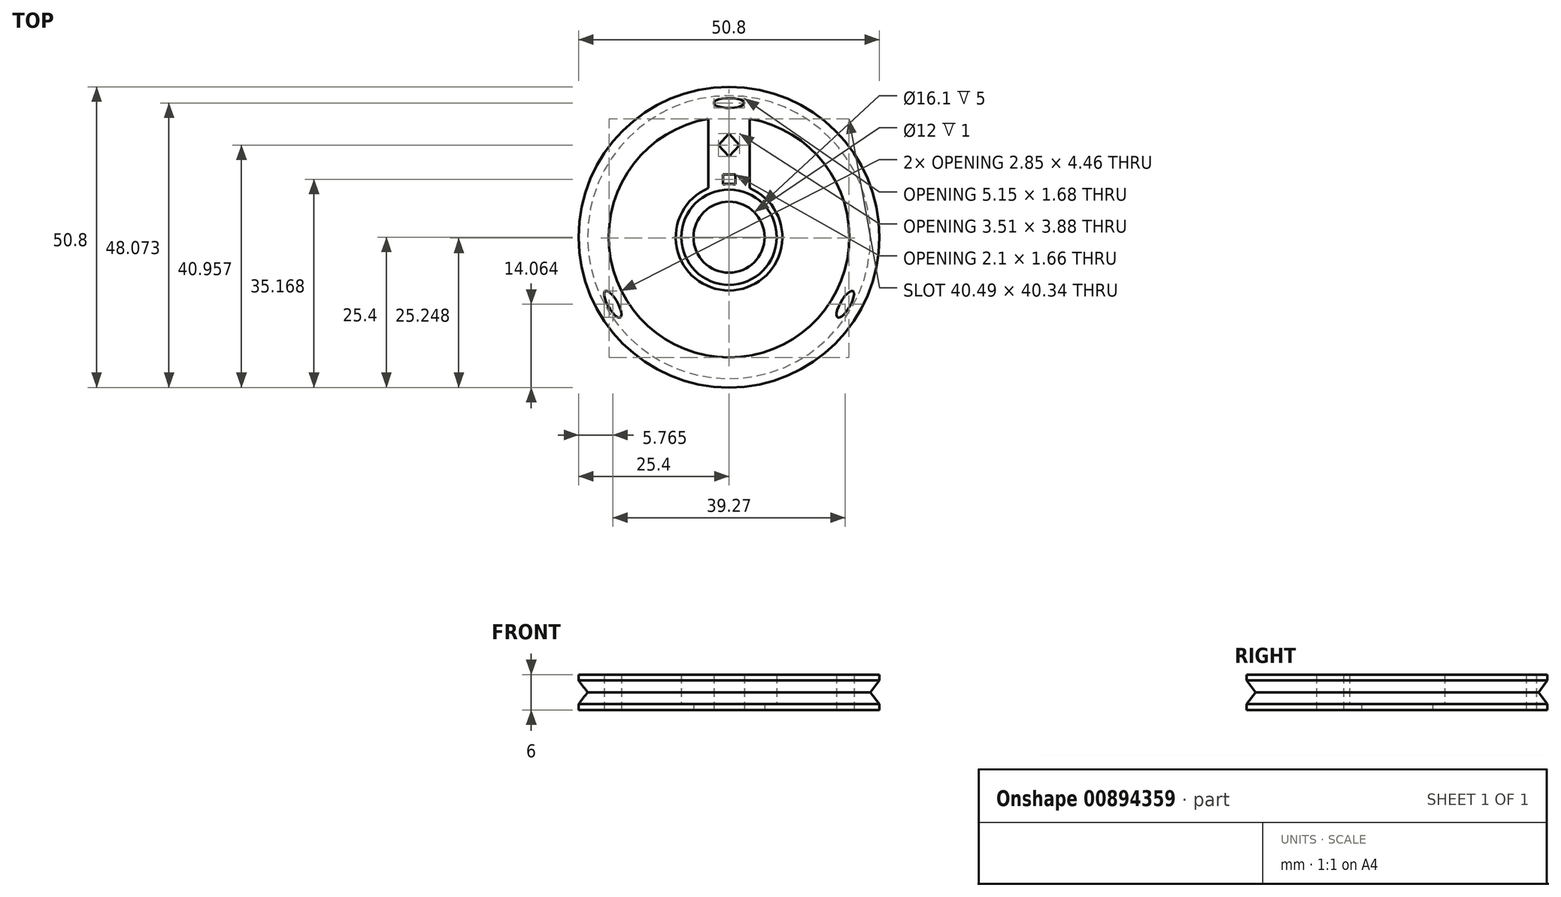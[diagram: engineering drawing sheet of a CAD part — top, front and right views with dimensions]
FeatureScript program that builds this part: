
annotation { "Feature Type Name" : "Feature", "Feature Type Description" : "" }
export const myFeature = defineFeature(function(context is Context, id is Id, definition is map)
    precondition{}
    {
        {
            var Q0;
            Q0=qCreatedBy(makeId("Top.planeOp"),FACE);
            var sketch = newSketch(context, id + "F0", { "sketchPlane" : qUnion([Q0])});
            skCircle(sketch, "E0", {"center": v(0, 0) * mm, "radius": 25.4 * mm});
            skCircle(sketch, "E1", {"center": v(0, 0) * mm, "radius": 6 * mm});
            skCircle(sketch, "E2.0", {"center": v(0, 0) * mm, "radius": 20.32 * mm});
            skLineSegment(sketch, "E3.left", {"start": v(3.5, 4.87) * mm, "end": v(3.5, 20.02) * mm});
            skLineSegment(sketch, "E3.right", {"start": v(-3.5, 4.87) * mm, "end": v(-3.5, 20.02) * mm});
            skPoint(sketch, "E3.middle", {"position": v(0, 12.94) * mm});
            skPoint(sketch, "E4.orphan", {"position": v(-3.5, 22.78) * mm});
            skPoint(sketch, "E5.orphan", {"position": v(3.5, 22.78) * mm});
            skPoint(sketch, "E6.orphan", {"position": v(-3.5, 3.1) * mm});
            skPoint(sketch, "E7.orphan", {"position": v(3.5, 3.1) * mm});
            skLineSegment(sketch, "E8", {"start": v(0, 15.56) * mm, "end": v(-1.76, 15.56) * mm});
            skLineSegment(sketch, "E9", {"start": v(-1.76, 15.56) * mm, "end": v(0, 17.5) * mm});
            skLineSegment(sketch, "E10", {"start": v(0, 17.5) * mm, "end": v(0, 15.56) * mm});
            skLineSegment(sketch, "E11.MirrorCS", {"start": v(0, 15.56) * mm, "end": v(1.76, 15.55) * mm});
            skLineSegment(sketch, "E12.MirrorCS", {"start": v(1.76, 15.55) * mm, "end": v(0, 17.5) * mm});
            skLineSegment(sketch, "E13.MirrorCS", {"start": v(-1.76, 15.56) * mm, "end": v(0, 13.61) * mm});
            skLineSegment(sketch, "E14.MirrorCS", {"start": v(0, 13.61) * mm, "end": v(0, 15.56) * mm});
            skLineSegment(sketch, "E15.MirrorCS", {"start": v(1.76, 15.55) * mm, "end": v(0, 13.61) * mm});
            skLineSegment(sketch, "E16.bottom", {"start": v(1.05, 10.6) * mm, "end": v(-1.05, 10.6) * mm});
            skLineSegment(sketch, "E16.top", {"start": v(1.05, 8.43) * mm, "end": v(-1.05, 8.43) * mm});
            skLineSegment(sketch, "E16.left", {"start": v(1.05, 10.6) * mm, "end": v(1.05, 8.43) * mm});
            skLineSegment(sketch, "E16.right", {"start": v(-1.05, 10.6) * mm, "end": v(-1.05, 8.43) * mm});
            skPoint(sketch, "E16.middle", {"position": v(0, 9.51) * mm});
            skPoint(sketch, "E17.center.orphan", {"position": v(0, 22.67) * mm});
            skEllipse(sketch, "E18", {"center": v(0, 22.67) * mm, "majorRadius": 2.58 * mm, "minorRadius": 0.84 * mm, "majorAxis": v(-1, 0)});
            skEllipse(sketch, "E19.1.0", {"center": v(-19.63, -11.34) * mm, "majorRadius": 2.58 * mm, "minorRadius": 0.84 * mm, "majorAxis": v(0.5, -0.87)});
            skLineSegment(sketch, "E19.1.1", {"start": v(-11.8, -6.8) * mm, "end": v(-13.47, -7.78) * mm});
            skLineSegment(sketch, "E19.1.2", {"start": v(-2.47, -5.47) * mm, "end": v(-15.58, -13.04) * mm});
            skLineSegment(sketch, "E19.1.3", {"start": v(-9.7, -4.4) * mm, "end": v(-7.82, -3.3) * mm});
            skLineSegment(sketch, "E19.1.4", {"start": v(-13.47, -7.78) * mm, "end": v(-14.35, -6.26) * mm});
            skLineSegment(sketch, "E19.1.5", {"start": v(-14.35, -6.26) * mm, "end": v(-11.79, -6.81) * mm});
            skLineSegment(sketch, "E19.1.6", {"start": v(-12.6, -9.3) * mm, "end": v(-11.8, -6.8) * mm});
            skLineSegment(sketch, "E19.1.7", {"start": v(-7.82, -3.3) * mm, "end": v(-6.78, -5.12) * mm});
            skLineSegment(sketch, "E19.1.8", {"start": v(-5.97, 0.6) * mm, "end": v(-19.08, -6.98) * mm});
            skLineSegment(sketch, "E19.1.9", {"start": v(-8.65, -6.2) * mm, "end": v(-6.78, -5.12) * mm});
            skLineSegment(sketch, "E19.1.10", {"start": v(-12.6, -9.3) * mm, "end": v(-15.16, -8.75) * mm});
            skLineSegment(sketch, "E19.1.11", {"start": v(-13.47, -7.78) * mm, "end": v(-12.6, -9.3) * mm});
            skLineSegment(sketch, "E19.1.12", {"start": v(-15.16, -8.75) * mm, "end": v(-13.47, -7.78) * mm});
            skLineSegment(sketch, "E19.1.13", {"start": v(-9.7, -4.4) * mm, "end": v(-8.65, -6.2) * mm});
            skLineSegment(sketch, "E19.1.14", {"start": v(-14.35, -6.26) * mm, "end": v(-15.16, -8.75) * mm});
            skEllipse(sketch, "E19.2.0", {"center": v(19.63, -11.34) * mm, "majorRadius": 2.58 * mm, "minorRadius": 0.84 * mm, "majorAxis": v(0.5, 0.87)});
            skLineSegment(sketch, "E19.2.1", {"start": v(11.79, -6.8) * mm, "end": v(13.47, -7.78) * mm});
            skLineSegment(sketch, "E19.2.2", {"start": v(5.97, 0.6) * mm, "end": v(19.08, -6.98) * mm});
            skLineSegment(sketch, "E19.2.3", {"start": v(8.65, -6.2) * mm, "end": v(6.78, -5.12) * mm});
            skLineSegment(sketch, "E19.2.4", {"start": v(13.47, -7.78) * mm, "end": v(12.6, -9.3) * mm});
            skLineSegment(sketch, "E19.2.5", {"start": v(12.6, -9.3) * mm, "end": v(11.8, -6.8) * mm});
            skLineSegment(sketch, "E19.2.6", {"start": v(14.35, -6.26) * mm, "end": v(11.79, -6.8) * mm});
            skLineSegment(sketch, "E19.2.7", {"start": v(6.78, -5.12) * mm, "end": v(7.82, -3.3) * mm});
            skLineSegment(sketch, "E19.2.8", {"start": v(2.47, -5.47) * mm, "end": v(15.58, -13.04) * mm});
            skLineSegment(sketch, "E19.2.9", {"start": v(9.7, -4.4) * mm, "end": v(7.82, -3.3) * mm});
            skLineSegment(sketch, "E19.2.10", {"start": v(14.35, -6.26) * mm, "end": v(15.15, -8.75) * mm});
            skLineSegment(sketch, "E19.2.11", {"start": v(13.47, -7.78) * mm, "end": v(14.35, -6.26) * mm});
            skLineSegment(sketch, "E19.2.12", {"start": v(15.15, -8.75) * mm, "end": v(13.47, -7.78) * mm});
            skLineSegment(sketch, "E19.2.13", {"start": v(8.65, -6.2) * mm, "end": v(9.7, -4.4) * mm});
            skLineSegment(sketch, "E19.2.14", {"start": v(12.6, -9.3) * mm, "end": v(15.15, -8.75) * mm});
            skSolve(sketch);
        }
        {
            var Q0;
            {var subQ8=sQuery(id+"F0.wireOp",EDGE,"E19.1.2");Q0=makeQuery(id+"F0.imprint","IMPRINT",FACE,{"disambiguationData":[TD([[makeQuery(id+"F0.imprint","IMPRINT",EDGE,{"derivedFrom":subQ8}),-1.0]])]});}
            var Q1;
            Q1=makeQuery(id+"F0.imprint","IMPRINT",FACE,{"disambiguationData":[TD([[makeQuery(id+"F0.imprint","IMPRINT",EDGE,{"derivedFrom":sQuery(id+"F0.wireOp",EDGE,"E0")}),1.0]])]});
            var Q2;
            {var subQ8=sQuery(id+"F0.wireOp",EDGE,"E3.left");Q2=makeQuery(id+"F0.imprint","IMPRINT",FACE,{"disambiguationData":[TD([[makeQuery(id+"F0.imprint","IMPRINT",EDGE,{"derivedFrom":subQ8}),1.0]])]});}
            var Q3;
            {var subQ7=sQuery(id+"F0.wireOp",EDGE,"E19.2.2");Q3=makeQuery(id+"F0.imprint","IMPRINT",FACE,{"disambiguationData":[TD([[makeQuery(id+"F0.imprint","IMPRINT",EDGE,{"derivedFrom":subQ7}),-1.0]])]});}
            var Q4;
            {var subQ0=sQuery(id+"F0.wireOp",EDGE,"E1");var subQ4=makeQuery(id+"F0.imprint","INTERSECT",VERTEX,{"derivedFrom":[subQ0,sQuery(id+"F0.wireOp",EDGE,"E3.left")]});Q4=makeQuery(id+"F0.imprint","IMPRINT",FACE,{"disambiguationData":[TD([[makeQuery(id+"F0.imprint","IMPRINT",EDGE,{"disambiguationData":[TD([[subQ4,1.0]])],"derivedFrom":subQ0}),1.0]])]});}
            extrude(context, id + "F1", {"entities" : qUnion([Q0, Q1, Q2, Q3, Q4]), "depth" : 6 * mm, "offsetDistance" : 25.4 * mm, "symmetric" : true});
        }
        {
            var Q0;
            Q0=qCreatedBy(makeId("Top.planeOp"),FACE);
            var sketch = newSketch(context, id + "F2", { "sketchPlane" : qUnion([Q0])});
            skCircle(sketch, "E20", {"center": v(0, 0) * mm, "radius": 9 * mm});
            skCircle(sketch, "E21", {"center": v(0, 0) * mm, "radius": 8.05 * mm});
            skSolve(sketch);
        }
        {
            var Q0;
            Q0=makeQuery(id+"F2.imprint","IMPRINT",FACE,{"disambiguationData":[TD([[makeQuery(id+"F2.imprint","IMPRINT",EDGE,{"derivedFrom":sQuery(id+"F2.wireOp",EDGE,"E20")}),1.0]])]});
            extrude(context, id + "F3", {"entities" : qUnion([Q0]), "operationType" : NewBodyOperationType.ADD, "depth" : 6 * mm, "offsetDistance" : 25.4 * mm, "symmetric" : true});
        }
        {
            var Q0;
            Q0=qCreatedBy(makeId("Top.planeOp"),FACE);
            var sketch = newSketch(context, id + "F4", { "sketchPlane" : qUnion([Q0])});
            skCircle(sketch, "E22", {"center": v(0, 0) * mm, "radius": 6 * mm});
            skSolve(sketch);
        }
        {
            var Q0;
            Q0 = qSketchRegion(id + "F4", true);
            extrude(context, id + "F5", {"entities" : qUnion([Q0]), "operationType" : NewBodyOperationType.REMOVE, "depth" : 25.4 * mm, "offsetDistance" : 25.4 * mm, "symmetric" : true});
        }
        {
            var Q0;
            Q0=makeQuery(id+"F3.boolean.opBoolean","MERGE",FACE,{"derivedFrom":[makeQuery(id+"F1.opExtrude","CAP_FACE",FACE,{"disambiguationData":[OSD([sQuery(id+"F0.wireOp",EDGE,"E0"),sQuery(id+"F0.wireOp",EDGE,"E1"),sQuery(id+"F0.wireOp",EDGE,"E2.0"),sQuery(id+"F0.wireOp",EDGE,"E3.left"),sQuery(id+"F0.wireOp",EDGE,"E3.right"),sQuery(id+"F0.wireOp",EDGE,"E9"),sQuery(id+"F0.wireOp",EDGE,"E12.MirrorCS"),sQuery(id+"F0.wireOp",EDGE,"E13.MirrorCS"),sQuery(id+"F0.wireOp",EDGE,"E14.MirrorCS"),sQuery(id+"F0.wireOp",EDGE,"E15.MirrorCS"),sQuery(id+"F0.wireOp",EDGE,"E16.bottom"),sQuery(id+"F0.wireOp",EDGE,"E16.top"),sQuery(id+"F0.wireOp",EDGE,"E16.left"),sQuery(id+"F0.wireOp",EDGE,"E16.right"),sQuery(id+"F0.wireOp",EDGE,"E18"),sQuery(id+"F0.wireOp",EDGE,"E19.1.0"),sQuery(id+"F0.wireOp",EDGE,"E19.1.1"),sQuery(id+"F0.wireOp",EDGE,"E19.1.2"),sQuery(id+"F0.wireOp",EDGE,"E19.1.3"),sQuery(id+"F0.wireOp",EDGE,"E19.1.5"),sQuery(id+"F0.wireOp",EDGE,"E19.1.6"),sQuery(id+"F0.wireOp",EDGE,"E19.1.7"),sQuery(id+"F0.wireOp",EDGE,"E19.1.8"),sQuery(id+"F0.wireOp",EDGE,"E19.1.9"),sQuery(id+"F0.wireOp",EDGE,"E19.1.10"),sQuery(id+"F0.wireOp",EDGE,"E19.1.13"),sQuery(id+"F0.wireOp",EDGE,"E19.1.14"),sQuery(id+"F0.wireOp",EDGE,"E19.2.0"),sQuery(id+"F0.wireOp",EDGE,"E19.2.1"),sQuery(id+"F0.wireOp",EDGE,"E19.2.2"),sQuery(id+"F0.wireOp",EDGE,"E19.2.3"),sQuery(id+"F0.wireOp",EDGE,"E19.2.5"),sQuery(id+"F0.wireOp",EDGE,"E19.2.6"),sQuery(id+"F0.wireOp",EDGE,"E19.2.7"),sQuery(id+"F0.wireOp",EDGE,"E19.2.8"),sQuery(id+"F0.wireOp",EDGE,"E19.2.9"),sQuery(id+"F0.wireOp",EDGE,"E19.2.10"),sQuery(id+"F0.wireOp",EDGE,"E19.2.13"),sQuery(id+"F0.wireOp",EDGE,"E19.2.14")])],"isStart":false}),makeQuery(id+"F3.opExtrude","CAP_FACE",FACE,{"disambiguationData":[OSD([sQuery(id+"F2.wireOp",EDGE,"E20"),sQuery(id+"F2.wireOp",EDGE,"E21")])],"isStart":false})]});
            var sketch = newSketch(context, id + "F6", { "sketchPlane" : qUnion([Q0])});
            skCircle(sketch, "E23", {"center": v(0, 0) * mm, "radius": 8.05 * mm});
            skCircle(sketch, "E24", {"center": v(0, 0) * mm, "radius": 6 * mm});
            skSolve(sketch);
        }
        {
            var Q0;
            Q0 = qSketchRegion(id + "F6", true);
            extrude(context, id + "F7", {"entities" : qUnion([Q0]), "operationType" : NewBodyOperationType.REMOVE, "oppositeDirection" : true, "depth" : 12 * mm, "offsetDistance" : 25.4 * mm});
        }
        {
            var Q0;
            Q0=makeQuery(id+"F3.boolean.opBoolean","MERGE",FACE,{"derivedFrom":[makeQuery(id+"F1.opExtrude","CAP_FACE",FACE,{"disambiguationData":[OSD([sQuery(id+"F0.wireOp",EDGE,"E0"),sQuery(id+"F0.wireOp",EDGE,"E1"),sQuery(id+"F0.wireOp",EDGE,"E2.0"),sQuery(id+"F0.wireOp",EDGE,"E3.left"),sQuery(id+"F0.wireOp",EDGE,"E3.right"),sQuery(id+"F0.wireOp",EDGE,"E9"),sQuery(id+"F0.wireOp",EDGE,"E12.MirrorCS"),sQuery(id+"F0.wireOp",EDGE,"E13.MirrorCS"),sQuery(id+"F0.wireOp",EDGE,"E14.MirrorCS"),sQuery(id+"F0.wireOp",EDGE,"E15.MirrorCS"),sQuery(id+"F0.wireOp",EDGE,"E16.bottom"),sQuery(id+"F0.wireOp",EDGE,"E16.top"),sQuery(id+"F0.wireOp",EDGE,"E16.left"),sQuery(id+"F0.wireOp",EDGE,"E16.right"),sQuery(id+"F0.wireOp",EDGE,"E18"),sQuery(id+"F0.wireOp",EDGE,"E19.1.0"),sQuery(id+"F0.wireOp",EDGE,"E19.1.1"),sQuery(id+"F0.wireOp",EDGE,"E19.1.2"),sQuery(id+"F0.wireOp",EDGE,"E19.1.3"),sQuery(id+"F0.wireOp",EDGE,"E19.1.5"),sQuery(id+"F0.wireOp",EDGE,"E19.1.6"),sQuery(id+"F0.wireOp",EDGE,"E19.1.7"),sQuery(id+"F0.wireOp",EDGE,"E19.1.8"),sQuery(id+"F0.wireOp",EDGE,"E19.1.9"),sQuery(id+"F0.wireOp",EDGE,"E19.1.10"),sQuery(id+"F0.wireOp",EDGE,"E19.1.13"),sQuery(id+"F0.wireOp",EDGE,"E19.1.14"),sQuery(id+"F0.wireOp",EDGE,"E19.2.0"),sQuery(id+"F0.wireOp",EDGE,"E19.2.1"),sQuery(id+"F0.wireOp",EDGE,"E19.2.2"),sQuery(id+"F0.wireOp",EDGE,"E19.2.3"),sQuery(id+"F0.wireOp",EDGE,"E19.2.5"),sQuery(id+"F0.wireOp",EDGE,"E19.2.6"),sQuery(id+"F0.wireOp",EDGE,"E19.2.7"),sQuery(id+"F0.wireOp",EDGE,"E19.2.8"),sQuery(id+"F0.wireOp",EDGE,"E19.2.9"),sQuery(id+"F0.wireOp",EDGE,"E19.2.10"),sQuery(id+"F0.wireOp",EDGE,"E19.2.13"),sQuery(id+"F0.wireOp",EDGE,"E19.2.14")])],"isStart":true}),makeQuery(id+"F3.opExtrude","CAP_FACE",FACE,{"disambiguationData":[OSD([sQuery(id+"F2.wireOp",EDGE,"E20"),sQuery(id+"F2.wireOp",EDGE,"E21")])],"isStart":true})]});
            var sketch = newSketch(context, id + "F8", { "sketchPlane" : qUnion([Q0])});
            skCircle(sketch, "E25", {"center": v(0, 0) * mm, "radius": 8.05 * mm});
            skCircle(sketch, "E26", {"center": v(0, 0) * mm, "radius": 6 * mm});
            skSolve(sketch);
        }
        {
            var Q0;
            Q0=makeQuery(id+"F8.imprint","IMPRINT",FACE,{"disambiguationData":[TD([[makeQuery(id+"F8.imprint","IMPRINT",EDGE,{"derivedFrom":sQuery(id+"F8.wireOp",EDGE,"E25")}),-1.0]])]});
            extrude(context, id + "F9", {"entities" : qUnion([Q0]), "operationType" : NewBodyOperationType.ADD, "oppositeDirection" : true, "depth" : 1 * mm, "offsetDistance" : 25.4 * mm});
        }
        {
            var Q0;
            Q0=qCreatedBy(makeId("Front.planeOp"),FACE);
            var sketch = newSketch(context, id + "F10", { "sketchPlane" : qUnion([Q0])});
            skLineSegment(sketch, "E27", {"start": v(-25.4, 0) * mm, "end": v(-23.9, 0) * mm});
            skLineSegment(sketch, "E28", {"start": v(-23.9, 0) * mm, "end": v(-25.4, -2) * mm});
            skLineSegment(sketch, "E29", {"start": v(-25.4, -2) * mm, "end": v(-25.4, 0) * mm});
            skLineSegment(sketch, "E30.MirrorCS", {"start": v(-23.9, 0) * mm, "end": v(-25.4, 2) * mm});
            skLineSegment(sketch, "E31.MirrorCS", {"start": v(-25.4, 2) * mm, "end": v(-25.4, 0) * mm});
            skLineSegment(sketch, "E32", {"start": v(0, 0) * mm, "end": v(0, -10.38) * mm, "construction": true});
            skSolve(sketch);
        }
        {
            var Q0;
            Q0=makeQuery(id+"F10.imprint","IMPRINT",FACE,{"disambiguationData":[TD([[makeQuery(id+"F10.imprint","IMPRINT",EDGE,{"derivedFrom":sQuery(id+"F10.wireOp",EDGE,"E27")}),1.0]])]});
            var Q1;
            Q1=makeQuery(id+"F10.imprint","IMPRINT",FACE,{"disambiguationData":[TD([[makeQuery(id+"F10.imprint","IMPRINT",EDGE,{"derivedFrom":sQuery(id+"F10.wireOp",EDGE,"E27")}),-1.0]])]});
            var Q2;
            Q2=sQuery(id+"F10.wireOp",EDGE,"E32");
            revolve(context, id + "F11", {"operationType" : NewBodyOperationType.REMOVE, "surfaceOperationType" : NewSurfaceOperationType.NEW, "entities" : qUnion([Q0, Q1]), "axis" : qUnion([Q2]), "revolveType" : RevolveType.FULL, "oppositeDirection" : true});
        }
    });
